# Revit family: Thorn ISARO PRO Small side entry 60mm
name_source: partatom
category: Lighting Fixtures
revit_build: Autodesk Revit 2016 (Build: 20150220_1215(x64)
units: mm (PartAtom-declared; Revit-internal decimal feet)

## family parameters
Always vertical = Yes
Cut with Voids When Loaded = No
Light Source = Yes
OmniClass Number = 23.80.70.14
OmniClass Title = Luminaries for External Lighting
Part Type = Normal
Room Calculation Point = No
Round Connector Dimension = Use Diameter
Shared = No
Work Plane-Based = Yes

## types (1)
- Isaro PRO Small side entry 60mm
    Apparent Load = 20 VA
    Color Filter = 16777215
    Default Elevation = 0 mm  [stored 0 ft]
    Description = LED road lighting luminaire
    Dimming Lamp Color Temperature Shift = <None>
    Emit Shape Visible in Rendering = No
    Emit from Rectangle Length = 230 mm  [stored 0.754593 ft]
    Emit from Rectangle Width = 194 mm  [stored 0.636483 ft]
    Height = 114 mm  [stored 0.374016 ft]
    Lamp = LED
    Length = 571 mm  [stored 1.87336 ft]
    Manufacturer = Thorn Lighting
    Model = 96276036
    Photometric Web File = 96276036_(STD).IES
    Tilt Angle = 90.00°
    URL = www.thornlighting.com/96276036
    Voltage = 230 V
    Width = 224 mm  [stored 0.734908 ft]

note: [stored X ft] marks values corroborated as IEEE doubles in the binary element streams (Revit-internal decimal feet)

## geometry (parser evidence)
native form markers: Sweep x6
no freeform markers — native parametric forms only
